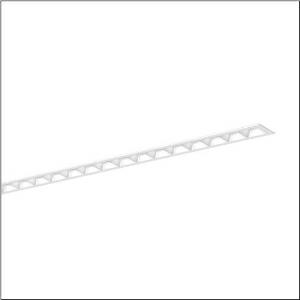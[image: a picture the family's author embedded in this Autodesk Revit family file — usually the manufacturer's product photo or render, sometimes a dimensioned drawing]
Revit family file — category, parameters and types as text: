
# Revit family: silica_21_51mx16dc3awb
name_source: partatom
category: Lighting Fixtures
units: mm (PartAtom-declared; Revit-internal decimal feet)

## family parameters
Cut with Voids When Loaded = No
Host = Face
Light Source = No
Part Type = Normal
Room Calculation Point = No
Round Connector Dimension = Use Diameter
Shared = No

## types (1)
- --- (1 x LED, 10800 lm, 63.6 W, 3000K)
    Apparent Load = 64 VA
    CIE Flux Codes = 83 98 100 100 100
    Color Rendering = 80
    Color Temperature = 3000K
    Default Elevation = 1800 mm
    Description = Silica 21, office luminaire, primary light control with darklight reflector, of PMMA, white, CAT 2 (L<= 3000cd/m²), light emission: direct distribution, primary light characteristic: symmetric, installation type: recessed, LED, rated luminous flux: 10.800lm, luminous efficacy: 170lm/W, light colour: 830, colour temperature: 3000K, control gear: DALI 2, with terminal, 3+2-pole, max. 2.5mm², mains connection: 220..240V, AC, 50/60Hz, rated input power: 63.6W, luminaire housing, of aluminium, traffic white (RAL 9016), length: 3.028mm, width: 79mm, height: 53mm, protection rating (complete): IP20, insulation class (complete): insulation class I (protective earthing), certification: CE, ENEC, VDE, permissible operating ambient temperature: 0..+35°C, standard: EN 50419, packaging unit: 1 piece
    Height = 0 mm  [stored 0 ft]
    Lamp = 1 x LED
    Lamp Light Flux = 10800 lm
    Lamp Power = 63.6 W
    Lamp count = 1
    Length = 3027 mm
    Luminous efficacy = 170 lm/W
    Manufacturer = Siteco
    ModVariant = No
    Model = 51MX16DC3AWB
    Mounting Place = Ceiling
    Mounting Type = Recessed
    Number of Poles = 1
    OnlyDefault = Yes
    Power Factor = 1
    Product Name = Silica 21
    Product group = office luminaire | ceiling recessed
    ProductGroupID = 400
    Protection Class = Protection class I
    Protection Degree = IP 20
    RLX_Detail_Level = 1
    RLX_Emergency_Light_Flux = 0 lm
    RLX_Emergency_Type = 0
    RLX_Emergency_Type_DB = No
    RlxData = <blob elided: 59821 chars, md5=c4820d2a>
    Socket = socket
    Standby Power = 0 W
    System Light Flux = 10800 lm
    System Power = 64 W
    Type Comments = factory setting: luminous flux: 100 % | dim-lin: 254 | 360 mA
    Type Image = l_1335884.jpg
    URL = http://relux.com
    VarID = @adj_124167
    Voltage = 0 V
    Weight = 0.00 kg
    Width = 79 mm

note: [stored X ft] marks values corroborated as IEEE doubles in the binary element streams (Revit-internal decimal feet)

## geometry (parser evidence)
native form markers: Blend x4, Sweep x12
no freeform markers — native parametric forms only
